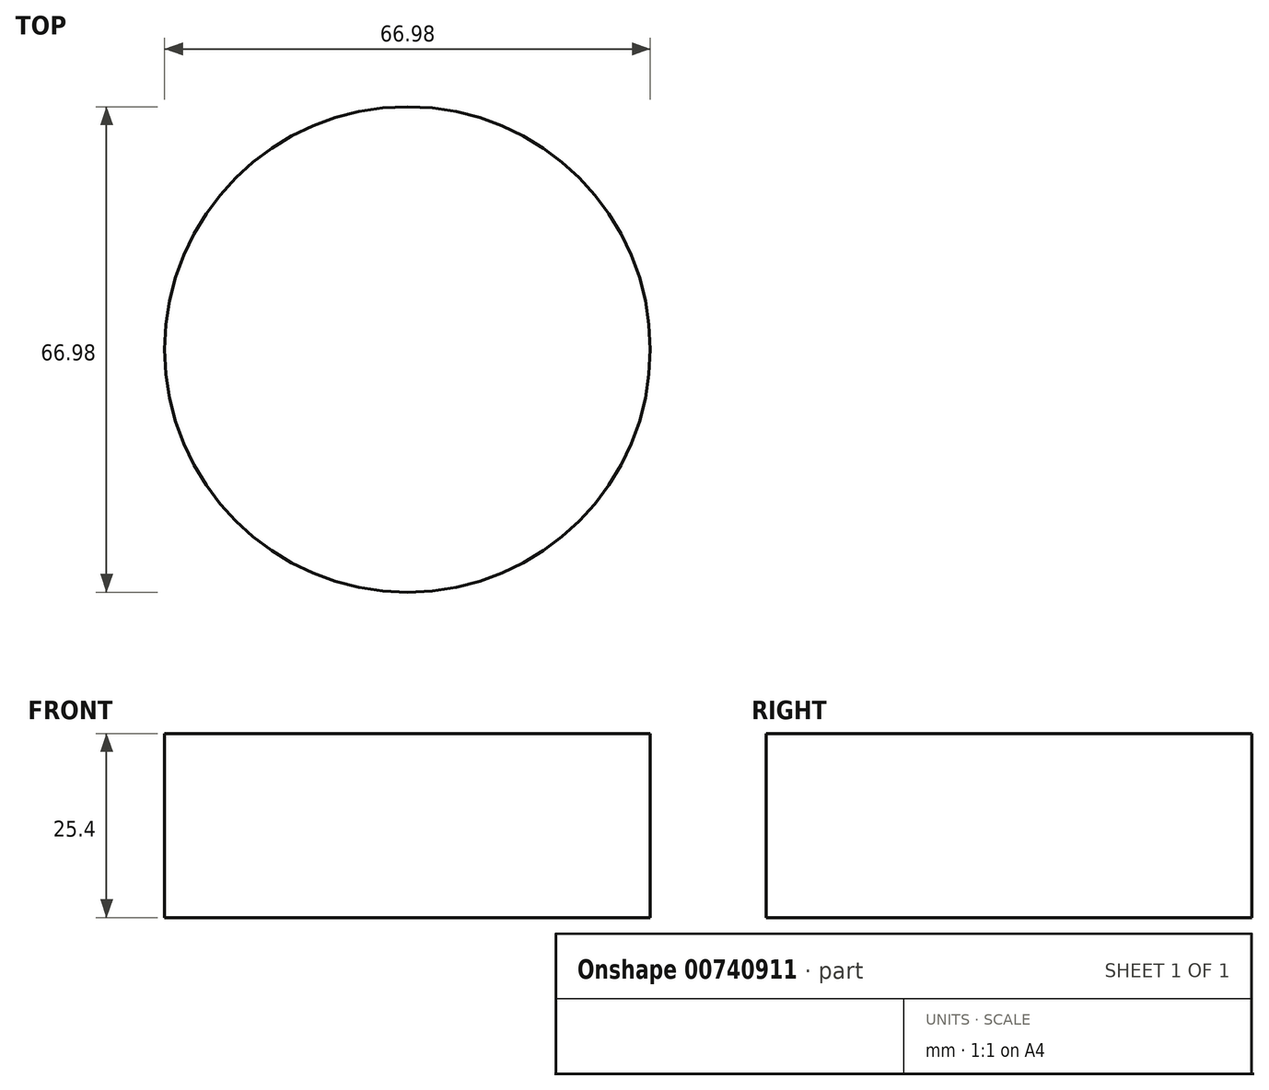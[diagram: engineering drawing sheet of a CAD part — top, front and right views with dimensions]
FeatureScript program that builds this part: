
annotation { "Feature Type Name" : "Feature", "Feature Type Description" : "" }
export const myFeature = defineFeature(function(context is Context, id is Id, definition is map)
    precondition{}
    {
        {
            var Q0;
            Q0=qCreatedBy(makeId("Top.planeOp"),FACE);
            var sketch = newSketch(context, id + "F0", { "sketchPlane" : qUnion([Q0])});
            skCircle(sketch, "E0", {"center": v(0, -13.18) * mm, "radius": 33.49 * mm});
            skSolve(sketch);
        }
        {
            var Q0;
            Q0 = qSketchRegion(id + "F0", true);
            extrude(context, id + "F1", {"entities" : qUnion([Q0]), "depth" : 25.4 * mm, "offsetDistance" : 25.4 * mm});
        }
    });
